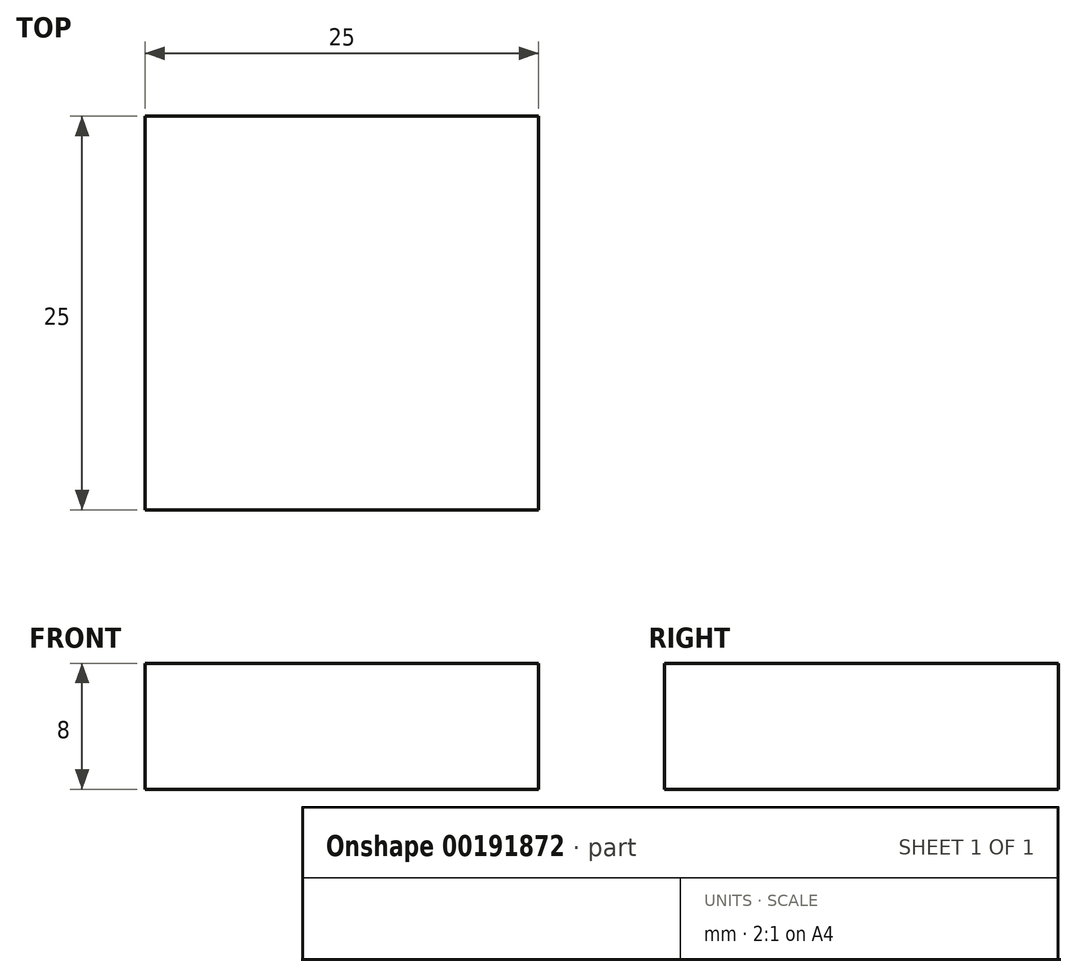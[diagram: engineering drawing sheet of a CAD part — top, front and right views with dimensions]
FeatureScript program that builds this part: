
annotation { "Feature Type Name" : "Feature", "Feature Type Description" : "" }
export const myFeature = defineFeature(function(context is Context, id is Id, definition is map)
    precondition{}
    {
        {
            var Q0;
            Q0=qCreatedBy(makeId("Top.planeOp"),FACE);
            var sketch = newSketch(context, id + "F0", { "sketchPlane" : qUnion([Q0])});
            skLineSegment(sketch, "E0.bottom", {"start": v(9.84, -12.5) * mm, "end": v(-15.16, -12.5) * mm});
            skLineSegment(sketch, "E0.top", {"start": v(9.84, 12.5) * mm, "end": v(-15.16, 12.5) * mm});
            skLineSegment(sketch, "E0.left", {"start": v(9.84, -12.5) * mm, "end": v(9.84, 12.5) * mm});
            skLineSegment(sketch, "E0.right", {"start": v(-15.16, -12.5) * mm, "end": v(-15.16, 12.5) * mm});
            skPoint(sketch, "E0.middle", {"position": v(-2.66, 0) * mm});
            skSolve(sketch);
        }
        {
            var Q0;
            Q0=makeQuery(id+"F0.imprint","IMPRINT",FACE,{"disambiguationData":[TD([[makeQuery(id+"F0.imprint","IMPRINT",EDGE,{"derivedFrom":sQuery(id+"F0.wireOp",EDGE,"E0.bottom")}),-1.0]])]});
            extrude(context, id + "F1", {"entities" : qUnion([Q0]), "depth" : 8 * mm});
        }
    });
